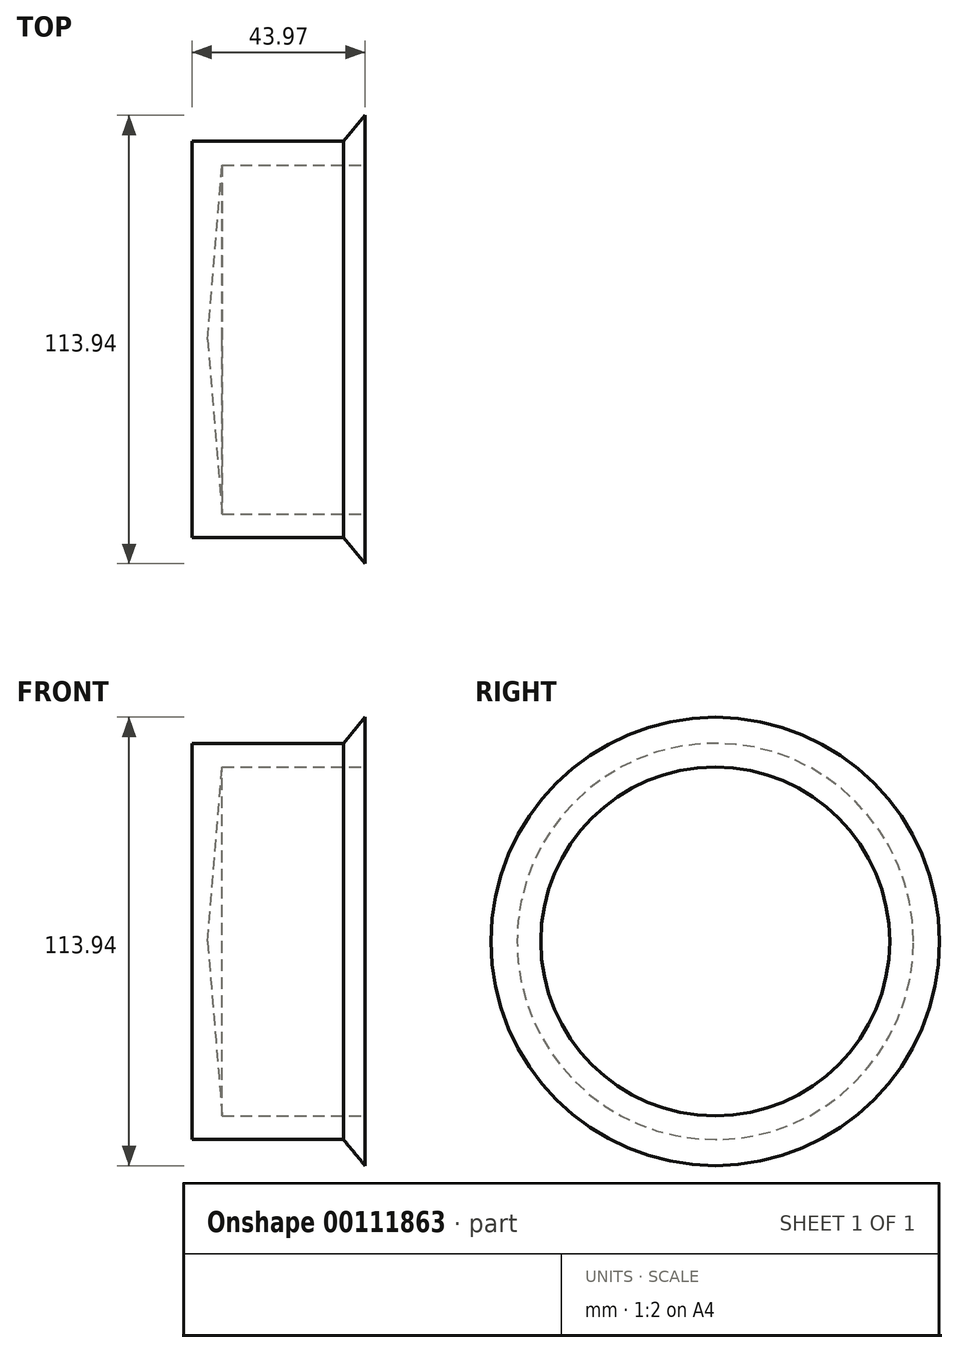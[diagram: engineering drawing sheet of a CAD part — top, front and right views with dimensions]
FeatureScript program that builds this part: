
annotation { "Feature Type Name" : "Feature", "Feature Type Description" : "" }
export const myFeature = defineFeature(function(context is Context, id is Id, definition is map)
    precondition{}
    {
        {
            var Q0;
            Q0=qCreatedBy(makeId("Front.planeOp"),FACE);
            var sketch = newSketch(context, id + "F0", { "sketchPlane" : qUnion([Q0])});
            skLineSegment(sketch, "E0", {"start": v(0, 0) * mm, "end": v(3.97, 0) * mm});
            skLineSegment(sketch, "E1", {"start": v(43.97, 44.32) * mm, "end": v(43.97, 56.97) * mm});
            skLineSegment(sketch, "E2", {"start": v(43.97, 56.97) * mm, "end": v(38.5, 50.34) * mm});
            skLineSegment(sketch, "E3", {"start": v(38.5, 50.34) * mm, "end": v(0, 50.34) * mm});
            skLineSegment(sketch, "E4", {"start": v(0, 50.34) * mm, "end": v(0, 0) * mm});
            skLineSegment(sketch, "E5", {"start": v(43.97, 44.32) * mm, "end": v(7.7, 44.32) * mm});
            skLineSegment(sketch, "E6", {"start": v(7.7, 44.32) * mm, "end": v(3.97, 0) * mm});
            skLineSegment(sketch, "E7", {"start": v(3.97, 0) * mm, "end": v(0, 0) * mm});
            skSolve(sketch);
        }
        {
            var Q0;
            Q0=makeQuery(id+"F0.imprint","IMPRINT",FACE,{"disambiguationData":[TD([[makeQuery(id+"F0.imprint","IMPRINT",EDGE,{"derivedFrom":sQuery(id+"F0.wireOp",EDGE,"E1")}),1.0]])]});
            var Q1;
            Q1=sQuery(id+"F0.wireOp",EDGE,"E7");
            revolve(context, id + "F1", {"entities" : qUnion([Q0]), "axis" : qUnion([Q1]), "revolveType" : RevolveType.FULL});
        }
    });
